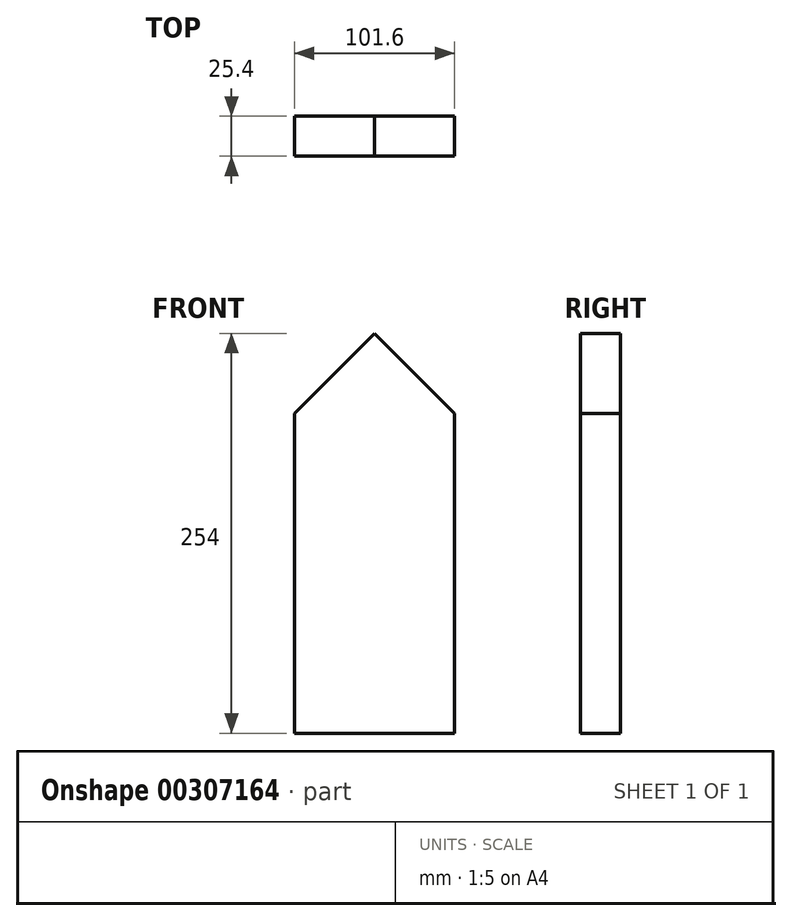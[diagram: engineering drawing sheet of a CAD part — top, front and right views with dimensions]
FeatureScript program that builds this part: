
annotation { "Feature Type Name" : "Feature", "Feature Type Description" : "" }
export const myFeature = defineFeature(function(context is Context, id is Id, definition is map)
    precondition{}
    {
        {
            var Q0;
            Q0=qCreatedBy(makeId("Front.planeOp"),FACE);
            var sketch = newSketch(context, id + "F0", { "sketchPlane" : qUnion([Q0])});
            skLineSegment(sketch, "E0", {"start": v(-45.3, -71.22) * mm, "end": v(56.3, -71.22) * mm});
            skLineSegment(sketch, "E1", {"start": v(56.3, -71.22) * mm, "end": v(56.3, 131.98) * mm});
            skLineSegment(sketch, "E2", {"start": v(-45.3, -71.22) * mm, "end": v(-45.3, 131.98) * mm});
            skLineSegment(sketch, "E3", {"start": v(-45.3, 131.98) * mm, "end": v(5.5, 182.78) * mm});
            skLineSegment(sketch, "E4", {"start": v(5.5, 182.78) * mm, "end": v(56.3, 131.98) * mm});
            skSolve(sketch);
        }
        {
            var Q0;
            Q0=makeQuery(id+"F0.imprint","IMPRINT",FACE,{"disambiguationData":[TD([[makeQuery(id+"F0.imprint","IMPRINT",EDGE,{"derivedFrom":sQuery(id+"F0.wireOp",EDGE,"E0")}),1.0]])]});
            extrude(context, id + "F1", {"entities" : qUnion([Q0]), "depth" : 25.4 * mm});
        }
    });
